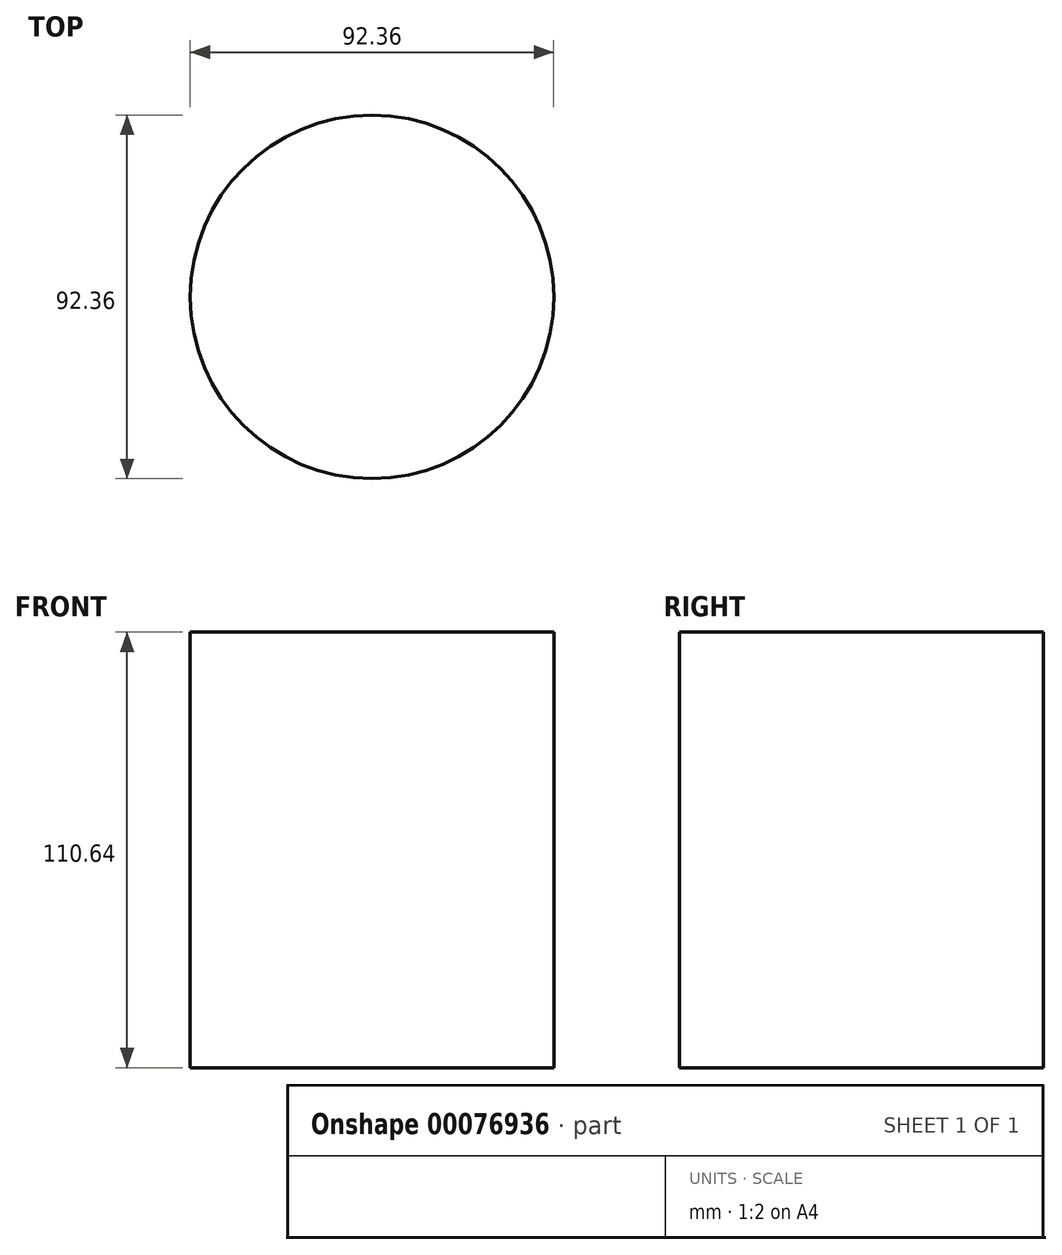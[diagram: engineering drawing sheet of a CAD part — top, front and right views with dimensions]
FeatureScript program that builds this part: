
annotation { "Feature Type Name" : "Feature", "Feature Type Description" : "" }
export const myFeature = defineFeature(function(context is Context, id is Id, definition is map)
    precondition{}
    {
        {
            var Q0;
            Q0=qCreatedBy(makeId("Front.planeOp"),FACE);
            var sketch = newSketch(context, id + "F0", { "sketchPlane" : qUnion([Q0])});
            skLineSegment(sketch, "E0.bottom", {"start": v(0, 56.58) * mm, "end": v(46.18, 56.58) * mm});
            skLineSegment(sketch, "E0.top", {"start": v(0, -54.06) * mm, "end": v(46.18, -54.06) * mm});
            skLineSegment(sketch, "E0.left", {"start": v(0, 56.58) * mm, "end": v(0, -54.06) * mm});
            skLineSegment(sketch, "E0.right", {"start": v(46.18, 56.58) * mm, "end": v(46.18, -54.06) * mm});
            skSolve(sketch);
        }
        {
            var Q0;
            Q0 = qSketchRegion(id + "F0", true);
            var Q1;
            Q1=sQuery(id+"F0.wireOp",EDGE,"E0.left");
            revolve(context, id + "F1", {"entities" : qUnion([Q0]), "axis" : qUnion([Q1]), "revolveType" : RevolveType.FULL});
        }
    });
